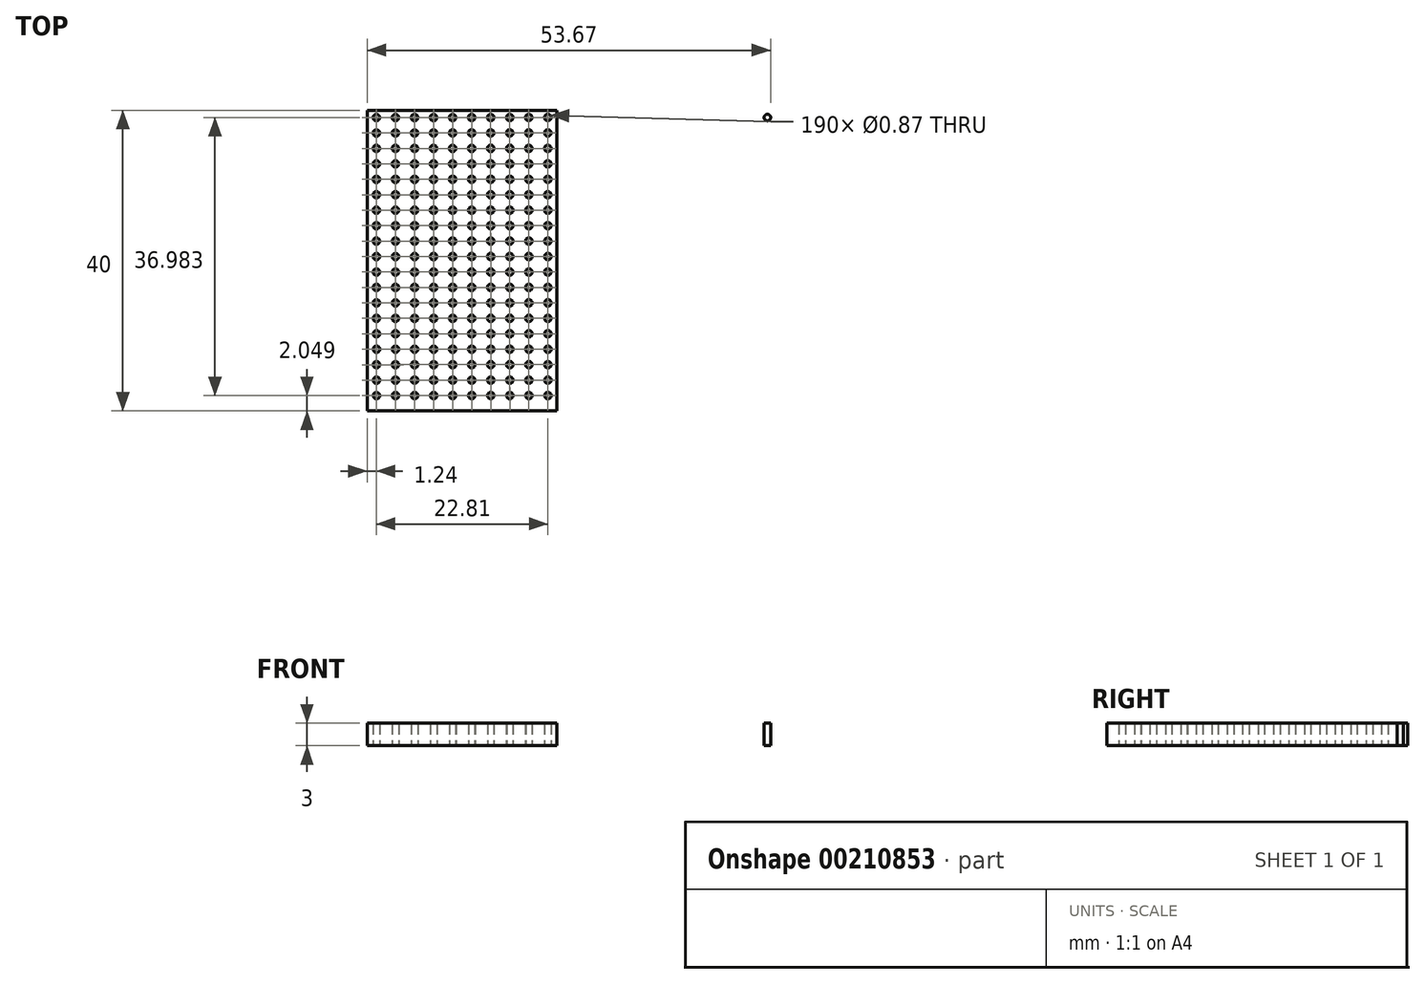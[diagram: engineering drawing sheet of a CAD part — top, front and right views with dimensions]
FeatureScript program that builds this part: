
annotation { "Feature Type Name" : "Feature", "Feature Type Description" : "" }
export const myFeature = defineFeature(function(context is Context, id is Id, definition is map)
    precondition{}
    {
        {
            var Q0;
            Q0=qCreatedBy(makeId("Top.planeOp"),FACE);
            var sketch = newSketch(context, id + "F0", { "sketchPlane" : qUnion([Q0])});
            skCircle(sketch, "E0", {"center": v(0, 0) * mm, "radius": 35 * mm, "construction": true});
            skLineSegment(sketch, "E1.bottom", {"start": v(-2, -20) * mm, "end": v(-27.24, -20) * mm});
            skLineSegment(sketch, "E1.top", {"start": v(-2, 20) * mm, "end": v(-27.24, 20) * mm});
            skLineSegment(sketch, "E1.left", {"start": v(-2, -20) * mm, "end": v(-2, 20) * mm});
            skLineSegment(sketch, "E1.right", {"start": v(-27.24, -20) * mm, "end": v(-27.24, 20) * mm});
            skPoint(sketch, "E1.middle", {"position": v(-14.62, 0) * mm});
            skPoint(sketch, "E2.middle", {"position": v(14.62, 0) * mm});
            skCircle(sketch, "E3", {"center": v(-26, 19.03) * mm, "radius": 0.43 * mm});
            skCircle(sketch, "E4.1.0.0", {"center": v(-23.47, 19.03) * mm, "radius": 0.43 * mm});
            skCircle(sketch, "E4.2.0.0", {"center": v(-20.93, 19.03) * mm, "radius": 0.43 * mm});
            skCircle(sketch, "E4.3.0.0", {"center": v(-18.4, 19.03) * mm, "radius": 0.43 * mm});
            skCircle(sketch, "E4.4.0.0", {"center": v(-15.87, 19.03) * mm, "radius": 0.43 * mm});
            skCircle(sketch, "E4.5.0.0", {"center": v(-13.33, 19.03) * mm, "radius": 0.43 * mm});
            skCircle(sketch, "E4.6.0.0", {"center": v(-10.8, 19.03) * mm, "radius": 0.43 * mm});
            skCircle(sketch, "E4.7.0.0", {"center": v(-8.27, 19.03) * mm, "radius": 0.43 * mm});
            skCircle(sketch, "E4.8.0.0", {"center": v(-5.74, 19.03) * mm, "radius": 0.43 * mm});
            skCircle(sketch, "E4.9.0.0", {"center": v(-3.2, 19.03) * mm, "radius": 0.43 * mm});
            skLineSegment(sketch, "E4.direction1", {"start": v(-26, 19.03) * mm, "end": v(-23.47, 19.03) * mm, "construction": true});
            skLineSegment(sketch, "E5.1.0.0", {"start": v(-26, 16.97) * mm, "end": v(-23.47, 16.97) * mm, "construction": true});
            skCircle(sketch, "E5.1.0.1", {"center": v(-8.27, 16.98) * mm, "radius": 0.43 * mm});
            skCircle(sketch, "E5.1.0.2", {"center": v(-3.2, 16.98) * mm, "radius": 0.43 * mm});
            skCircle(sketch, "E5.1.0.3", {"center": v(-18.4, 16.97) * mm, "radius": 0.43 * mm});
            skCircle(sketch, "E5.1.0.4", {"center": v(-20.93, 16.97) * mm, "radius": 0.43 * mm});
            skCircle(sketch, "E5.1.0.5", {"center": v(-5.73, 16.98) * mm, "radius": 0.43 * mm});
            skCircle(sketch, "E5.1.0.6", {"center": v(-10.8, 16.98) * mm, "radius": 0.43 * mm});
            skCircle(sketch, "E5.1.0.7", {"center": v(-13.33, 16.97) * mm, "radius": 0.43 * mm});
            skCircle(sketch, "E5.1.0.8", {"center": v(-15.87, 16.97) * mm, "radius": 0.43 * mm});
            skCircle(sketch, "E5.1.0.9", {"center": v(-23.47, 16.97) * mm, "radius": 0.43 * mm});
            skCircle(sketch, "E5.1.0.10", {"center": v(-26, 16.97) * mm, "radius": 0.43 * mm});
            skLineSegment(sketch, "E5.2.0.0", {"start": v(-26, 14.92) * mm, "end": v(-23.47, 14.92) * mm, "construction": true});
            skCircle(sketch, "E5.2.0.1", {"center": v(-8.27, 14.92) * mm, "radius": 0.43 * mm});
            skCircle(sketch, "E5.2.0.2", {"center": v(-3.2, 14.92) * mm, "radius": 0.43 * mm});
            skCircle(sketch, "E5.2.0.3", {"center": v(-18.4, 14.92) * mm, "radius": 0.43 * mm});
            skCircle(sketch, "E5.2.0.4", {"center": v(-20.93, 14.92) * mm, "radius": 0.43 * mm});
            skCircle(sketch, "E5.2.0.5", {"center": v(-5.73, 14.92) * mm, "radius": 0.43 * mm});
            skCircle(sketch, "E5.2.0.6", {"center": v(-10.8, 14.92) * mm, "radius": 0.43 * mm});
            skCircle(sketch, "E5.2.0.7", {"center": v(-13.33, 14.92) * mm, "radius": 0.43 * mm});
            skCircle(sketch, "E5.2.0.8", {"center": v(-15.87, 14.92) * mm, "radius": 0.43 * mm});
            skCircle(sketch, "E5.2.0.9", {"center": v(-23.47, 14.92) * mm, "radius": 0.43 * mm});
            skCircle(sketch, "E5.2.0.10", {"center": v(-26, 14.92) * mm, "radius": 0.43 * mm});
            skLineSegment(sketch, "E5.3.0.0", {"start": v(-26, 12.86) * mm, "end": v(-23.47, 12.86) * mm, "construction": true});
            skCircle(sketch, "E5.3.0.1", {"center": v(-8.27, 12.87) * mm, "radius": 0.43 * mm});
            skCircle(sketch, "E5.3.0.2", {"center": v(-3.2, 12.87) * mm, "radius": 0.43 * mm});
            skCircle(sketch, "E5.3.0.3", {"center": v(-18.4, 12.87) * mm, "radius": 0.43 * mm});
            skCircle(sketch, "E5.3.0.4", {"center": v(-20.93, 12.86) * mm, "radius": 0.43 * mm});
            skCircle(sketch, "E5.3.0.5", {"center": v(-5.73, 12.87) * mm, "radius": 0.43 * mm});
            skCircle(sketch, "E5.3.0.6", {"center": v(-10.8, 12.87) * mm, "radius": 0.43 * mm});
            skCircle(sketch, "E5.3.0.7", {"center": v(-13.33, 12.87) * mm, "radius": 0.43 * mm});
            skCircle(sketch, "E5.3.0.8", {"center": v(-15.87, 12.87) * mm, "radius": 0.43 * mm});
            skCircle(sketch, "E5.3.0.9", {"center": v(-23.47, 12.86) * mm, "radius": 0.43 * mm});
            skCircle(sketch, "E5.3.0.10", {"center": v(-26, 12.86) * mm, "radius": 0.43 * mm});
            skLineSegment(sketch, "E5.4.0.0", {"start": v(-26, 10.8) * mm, "end": v(-23.46, 10.8) * mm, "construction": true});
            skCircle(sketch, "E5.4.0.1", {"center": v(-8.27, 10.81) * mm, "radius": 0.43 * mm});
            skCircle(sketch, "E5.4.0.2", {"center": v(-3.2, 10.81) * mm, "radius": 0.43 * mm});
            skCircle(sketch, "E5.4.0.3", {"center": v(-18.4, 10.81) * mm, "radius": 0.43 * mm});
            skCircle(sketch, "E5.4.0.4", {"center": v(-20.93, 10.81) * mm, "radius": 0.43 * mm});
            skCircle(sketch, "E5.4.0.5", {"center": v(-5.73, 10.81) * mm, "radius": 0.43 * mm});
            skCircle(sketch, "E5.4.0.6", {"center": v(-10.8, 10.81) * mm, "radius": 0.43 * mm});
            skCircle(sketch, "E5.4.0.7", {"center": v(-13.33, 10.81) * mm, "radius": 0.43 * mm});
            skCircle(sketch, "E5.4.0.8", {"center": v(-15.87, 10.81) * mm, "radius": 0.43 * mm});
            skCircle(sketch, "E5.4.0.9", {"center": v(-23.46, 10.8) * mm, "radius": 0.43 * mm});
            skCircle(sketch, "E5.4.0.10", {"center": v(-26, 10.8) * mm, "radius": 0.43 * mm});
            skLineSegment(sketch, "E5.5.0.0", {"start": v(-26, 8.76) * mm, "end": v(-23.46, 8.76) * mm, "construction": true});
            skCircle(sketch, "E5.5.0.1", {"center": v(-8.27, 8.76) * mm, "radius": 0.43 * mm});
            skCircle(sketch, "E5.5.0.2", {"center": v(-3.2, 8.76) * mm, "radius": 0.43 * mm});
            skCircle(sketch, "E5.5.0.3", {"center": v(-18.4, 8.76) * mm, "radius": 0.43 * mm});
            skCircle(sketch, "E5.5.0.4", {"center": v(-20.93, 8.76) * mm, "radius": 0.43 * mm});
            skCircle(sketch, "E5.5.0.5", {"center": v(-5.73, 8.76) * mm, "radius": 0.43 * mm});
            skCircle(sketch, "E5.5.0.6", {"center": v(-10.8, 8.76) * mm, "radius": 0.43 * mm});
            skCircle(sketch, "E5.5.0.7", {"center": v(-13.33, 8.76) * mm, "radius": 0.43 * mm});
            skCircle(sketch, "E5.5.0.8", {"center": v(-15.86, 8.76) * mm, "radius": 0.43 * mm});
            skCircle(sketch, "E5.5.0.9", {"center": v(-23.46, 8.76) * mm, "radius": 0.43 * mm});
            skCircle(sketch, "E5.5.0.10", {"center": v(-26, 8.76) * mm, "radius": 0.43 * mm});
            skLineSegment(sketch, "E5.6.0.0", {"start": v(-26, 6.7) * mm, "end": v(-23.46, 6.7) * mm, "construction": true});
            skCircle(sketch, "E5.6.0.1", {"center": v(-8.26, 6.7) * mm, "radius": 0.43 * mm});
            skCircle(sketch, "E5.6.0.2", {"center": v(-3.2, 6.7) * mm, "radius": 0.43 * mm});
            skCircle(sketch, "E5.6.0.3", {"center": v(-18.4, 6.7) * mm, "radius": 0.43 * mm});
            skCircle(sketch, "E5.6.0.4", {"center": v(-20.93, 6.7) * mm, "radius": 0.43 * mm});
            skCircle(sketch, "E5.6.0.5", {"center": v(-5.73, 6.7) * mm, "radius": 0.43 * mm});
            skCircle(sketch, "E5.6.0.6", {"center": v(-10.8, 6.7) * mm, "radius": 0.43 * mm});
            skCircle(sketch, "E5.6.0.7", {"center": v(-13.33, 6.7) * mm, "radius": 0.43 * mm});
            skCircle(sketch, "E5.6.0.8", {"center": v(-15.86, 6.7) * mm, "radius": 0.43 * mm});
            skCircle(sketch, "E5.6.0.9", {"center": v(-23.46, 6.7) * mm, "radius": 0.43 * mm});
            skCircle(sketch, "E5.6.0.10", {"center": v(-26, 6.7) * mm, "radius": 0.43 * mm});
            skLineSegment(sketch, "E5.7.0.0", {"start": v(-26, 4.65) * mm, "end": v(-23.46, 4.65) * mm, "construction": true});
            skCircle(sketch, "E5.7.0.1", {"center": v(-8.26, 4.65) * mm, "radius": 0.43 * mm});
            skCircle(sketch, "E5.7.0.2", {"center": v(-3.2, 4.65) * mm, "radius": 0.43 * mm});
            skCircle(sketch, "E5.7.0.3", {"center": v(-18.4, 4.65) * mm, "radius": 0.43 * mm});
            skCircle(sketch, "E5.7.0.4", {"center": v(-20.93, 4.65) * mm, "radius": 0.43 * mm});
            skCircle(sketch, "E5.7.0.5", {"center": v(-5.73, 4.65) * mm, "radius": 0.43 * mm});
            skCircle(sketch, "E5.7.0.6", {"center": v(-10.8, 4.65) * mm, "radius": 0.43 * mm});
            skCircle(sketch, "E5.7.0.7", {"center": v(-13.33, 4.65) * mm, "radius": 0.43 * mm});
            skCircle(sketch, "E5.7.0.8", {"center": v(-15.86, 4.65) * mm, "radius": 0.43 * mm});
            skCircle(sketch, "E5.7.0.9", {"center": v(-23.46, 4.65) * mm, "radius": 0.43 * mm});
            skCircle(sketch, "E5.7.0.10", {"center": v(-26, 4.65) * mm, "radius": 0.43 * mm});
            skLineSegment(sketch, "E5.8.0.0", {"start": v(-26, 2.6) * mm, "end": v(-23.46, 2.6) * mm, "construction": true});
            skCircle(sketch, "E5.8.0.1", {"center": v(-8.26, 2.6) * mm, "radius": 0.43 * mm});
            skCircle(sketch, "E5.8.0.2", {"center": v(-3.2, 2.6) * mm, "radius": 0.43 * mm});
            skCircle(sketch, "E5.8.0.3", {"center": v(-18.4, 2.6) * mm, "radius": 0.43 * mm});
            skCircle(sketch, "E5.8.0.4", {"center": v(-20.93, 2.6) * mm, "radius": 0.43 * mm});
            skCircle(sketch, "E5.8.0.5", {"center": v(-5.73, 2.6) * mm, "radius": 0.43 * mm});
            skCircle(sketch, "E5.8.0.6", {"center": v(-10.8, 2.6) * mm, "radius": 0.43 * mm});
            skCircle(sketch, "E5.8.0.7", {"center": v(-13.33, 2.6) * mm, "radius": 0.43 * mm});
            skCircle(sketch, "E5.8.0.8", {"center": v(-15.86, 2.6) * mm, "radius": 0.43 * mm});
            skCircle(sketch, "E5.8.0.9", {"center": v(-23.46, 2.6) * mm, "radius": 0.43 * mm});
            skCircle(sketch, "E5.8.0.10", {"center": v(-26, 2.6) * mm, "radius": 0.43 * mm});
            skLineSegment(sketch, "E5.9.0.0", {"start": v(-26, 0.54) * mm, "end": v(-23.46, 0.54) * mm, "construction": true});
            skCircle(sketch, "E5.9.0.1", {"center": v(-8.26, 0.54) * mm, "radius": 0.43 * mm});
            skCircle(sketch, "E5.9.0.2", {"center": v(-3.2, 0.54) * mm, "radius": 0.43 * mm});
            skCircle(sketch, "E5.9.0.3", {"center": v(-18.4, 0.54) * mm, "radius": 0.43 * mm});
            skCircle(sketch, "E5.9.0.4", {"center": v(-20.93, 0.54) * mm, "radius": 0.43 * mm});
            skCircle(sketch, "E5.9.0.5", {"center": v(-5.73, 0.54) * mm, "radius": 0.43 * mm});
            skCircle(sketch, "E5.9.0.6", {"center": v(-10.8, 0.54) * mm, "radius": 0.43 * mm});
            skCircle(sketch, "E5.9.0.7", {"center": v(-13.33, 0.54) * mm, "radius": 0.43 * mm});
            skCircle(sketch, "E5.9.0.8", {"center": v(-15.86, 0.54) * mm, "radius": 0.43 * mm});
            skCircle(sketch, "E5.9.0.9", {"center": v(-23.46, 0.54) * mm, "radius": 0.43 * mm});
            skCircle(sketch, "E5.9.0.10", {"center": v(-26, 0.54) * mm, "radius": 0.43 * mm});
            skLineSegment(sketch, "E5.10.0.0", {"start": v(-26, -1.52) * mm, "end": v(-23.46, -1.52) * mm, "construction": true});
            skCircle(sketch, "E5.10.0.1", {"center": v(-8.26, -1.51) * mm, "radius": 0.43 * mm});
            skCircle(sketch, "E5.10.0.2", {"center": v(-3.2, -1.51) * mm, "radius": 0.43 * mm});
            skCircle(sketch, "E5.10.0.3", {"center": v(-18.4, -1.51) * mm, "radius": 0.43 * mm});
            skCircle(sketch, "E5.10.0.4", {"center": v(-20.93, -1.52) * mm, "radius": 0.43 * mm});
            skCircle(sketch, "E5.10.0.5", {"center": v(-5.73, -1.51) * mm, "radius": 0.43 * mm});
            skCircle(sketch, "E5.10.0.6", {"center": v(-10.8, -1.51) * mm, "radius": 0.43 * mm});
            skCircle(sketch, "E5.10.0.7", {"center": v(-13.33, -1.51) * mm, "radius": 0.43 * mm});
            skCircle(sketch, "E5.10.0.8", {"center": v(-15.86, -1.51) * mm, "radius": 0.43 * mm});
            skCircle(sketch, "E5.10.0.9", {"center": v(-23.46, -1.52) * mm, "radius": 0.43 * mm});
            skCircle(sketch, "E5.10.0.10", {"center": v(-26, -1.52) * mm, "radius": 0.43 * mm});
            skLineSegment(sketch, "E5.11.0.0", {"start": v(-26, -3.57) * mm, "end": v(-23.46, -3.57) * mm, "construction": true});
            skCircle(sketch, "E5.11.0.1", {"center": v(-8.26, -3.57) * mm, "radius": 0.43 * mm});
            skCircle(sketch, "E5.11.0.2", {"center": v(-3.2, -3.57) * mm, "radius": 0.43 * mm});
            skCircle(sketch, "E5.11.0.3", {"center": v(-18.4, -3.57) * mm, "radius": 0.43 * mm});
            skCircle(sketch, "E5.11.0.4", {"center": v(-20.93, -3.57) * mm, "radius": 0.43 * mm});
            skCircle(sketch, "E5.11.0.5", {"center": v(-5.73, -3.57) * mm, "radius": 0.43 * mm});
            skCircle(sketch, "E5.11.0.6", {"center": v(-10.8, -3.57) * mm, "radius": 0.43 * mm});
            skCircle(sketch, "E5.11.0.7", {"center": v(-13.33, -3.57) * mm, "radius": 0.43 * mm});
            skCircle(sketch, "E5.11.0.8", {"center": v(-15.86, -3.57) * mm, "radius": 0.43 * mm});
            skCircle(sketch, "E5.11.0.9", {"center": v(-23.46, -3.57) * mm, "radius": 0.43 * mm});
            skCircle(sketch, "E5.11.0.10", {"center": v(-26, -3.57) * mm, "radius": 0.43 * mm});
            skLineSegment(sketch, "E5.12.0.0", {"start": v(-26, -5.63) * mm, "end": v(-23.46, -5.62) * mm, "construction": true});
            skCircle(sketch, "E5.12.0.1", {"center": v(-8.26, -5.62) * mm, "radius": 0.43 * mm});
            skCircle(sketch, "E5.12.0.2", {"center": v(-3.2, -5.62) * mm, "radius": 0.43 * mm});
            skCircle(sketch, "E5.12.0.3", {"center": v(-18.4, -5.62) * mm, "radius": 0.43 * mm});
            skCircle(sketch, "E5.12.0.4", {"center": v(-20.93, -5.62) * mm, "radius": 0.43 * mm});
            skCircle(sketch, "E5.12.0.5", {"center": v(-5.73, -5.62) * mm, "radius": 0.43 * mm});
            skCircle(sketch, "E5.12.0.6", {"center": v(-10.8, -5.62) * mm, "radius": 0.43 * mm});
            skCircle(sketch, "E5.12.0.7", {"center": v(-13.33, -5.62) * mm, "radius": 0.43 * mm});
            skCircle(sketch, "E5.12.0.8", {"center": v(-15.86, -5.62) * mm, "radius": 0.43 * mm});
            skCircle(sketch, "E5.12.0.9", {"center": v(-23.46, -5.62) * mm, "radius": 0.43 * mm});
            skCircle(sketch, "E5.12.0.10", {"center": v(-26, -5.63) * mm, "radius": 0.43 * mm});
            skLineSegment(sketch, "E5.13.0.0", {"start": v(-26, -7.68) * mm, "end": v(-23.46, -7.68) * mm, "construction": true});
            skCircle(sketch, "E5.13.0.1", {"center": v(-8.26, -7.68) * mm, "radius": 0.43 * mm});
            skCircle(sketch, "E5.13.0.2", {"center": v(-3.2, -7.67) * mm, "radius": 0.43 * mm});
            skCircle(sketch, "E5.13.0.3", {"center": v(-18.4, -7.68) * mm, "radius": 0.43 * mm});
            skCircle(sketch, "E5.13.0.4", {"center": v(-20.93, -7.68) * mm, "radius": 0.43 * mm});
            skCircle(sketch, "E5.13.0.5", {"center": v(-5.73, -7.68) * mm, "radius": 0.43 * mm});
            skCircle(sketch, "E5.13.0.6", {"center": v(-10.8, -7.68) * mm, "radius": 0.43 * mm});
            skCircle(sketch, "E5.13.0.7", {"center": v(-13.33, -7.68) * mm, "radius": 0.43 * mm});
            skCircle(sketch, "E5.13.0.8", {"center": v(-15.86, -7.68) * mm, "radius": 0.43 * mm});
            skCircle(sketch, "E5.13.0.9", {"center": v(-23.46, -7.68) * mm, "radius": 0.43 * mm});
            skCircle(sketch, "E5.13.0.10", {"center": v(-26, -7.68) * mm, "radius": 0.43 * mm});
            skLineSegment(sketch, "E5.14.0.0", {"start": v(-26, -9.73) * mm, "end": v(-23.46, -9.73) * mm, "construction": true});
            skCircle(sketch, "E5.14.0.1", {"center": v(-8.26, -9.73) * mm, "radius": 0.43 * mm});
            skCircle(sketch, "E5.14.0.2", {"center": v(-3.2, -9.73) * mm, "radius": 0.43 * mm});
            skCircle(sketch, "E5.14.0.3", {"center": v(-18.4, -9.73) * mm, "radius": 0.43 * mm});
            skCircle(sketch, "E5.14.0.4", {"center": v(-20.92, -9.73) * mm, "radius": 0.43 * mm});
            skCircle(sketch, "E5.14.0.5", {"center": v(-5.73, -9.73) * mm, "radius": 0.43 * mm});
            skCircle(sketch, "E5.14.0.6", {"center": v(-10.8, -9.73) * mm, "radius": 0.43 * mm});
            skCircle(sketch, "E5.14.0.7", {"center": v(-13.33, -9.73) * mm, "radius": 0.43 * mm});
            skCircle(sketch, "E5.14.0.8", {"center": v(-15.86, -9.73) * mm, "radius": 0.43 * mm});
            skCircle(sketch, "E5.14.0.9", {"center": v(-23.46, -9.73) * mm, "radius": 0.43 * mm});
            skCircle(sketch, "E5.14.0.10", {"center": v(-26, -9.73) * mm, "radius": 0.43 * mm});
            skLineSegment(sketch, "E5.15.0.0", {"start": v(-25.99, -11.79) * mm, "end": v(-23.46, -11.79) * mm, "construction": true});
            skCircle(sketch, "E5.15.0.1", {"center": v(-8.26, -11.78) * mm, "radius": 0.43 * mm});
            skCircle(sketch, "E5.15.0.2", {"center": v(-3.2, -11.78) * mm, "radius": 0.43 * mm});
            skCircle(sketch, "E5.15.0.3", {"center": v(-18.4, -11.79) * mm, "radius": 0.43 * mm});
            skCircle(sketch, "E5.15.0.4", {"center": v(-20.92, -11.79) * mm, "radius": 0.43 * mm});
            skCircle(sketch, "E5.15.0.5", {"center": v(-5.73, -11.78) * mm, "radius": 0.43 * mm});
            skCircle(sketch, "E5.15.0.6", {"center": v(-10.8, -11.78) * mm, "radius": 0.43 * mm});
            skCircle(sketch, "E5.15.0.7", {"center": v(-13.32, -11.79) * mm, "radius": 0.43 * mm});
            skCircle(sketch, "E5.15.0.8", {"center": v(-15.86, -11.79) * mm, "radius": 0.43 * mm});
            skCircle(sketch, "E5.15.0.9", {"center": v(-23.46, -11.79) * mm, "radius": 0.43 * mm});
            skCircle(sketch, "E5.15.0.10", {"center": v(-25.99, -11.79) * mm, "radius": 0.43 * mm});
            skLineSegment(sketch, "E5.16.0.0", {"start": v(-25.99, -13.84) * mm, "end": v(-23.46, -13.84) * mm, "construction": true});
            skCircle(sketch, "E5.16.0.1", {"center": v(-8.26, -13.84) * mm, "radius": 0.43 * mm});
            skCircle(sketch, "E5.16.0.2", {"center": v(-3.2, -13.84) * mm, "radius": 0.43 * mm});
            skCircle(sketch, "E5.16.0.3", {"center": v(-18.39, -13.84) * mm, "radius": 0.43 * mm});
            skCircle(sketch, "E5.16.0.4", {"center": v(-20.92, -13.84) * mm, "radius": 0.43 * mm});
            skCircle(sketch, "E5.16.0.5", {"center": v(-5.72, -13.84) * mm, "radius": 0.43 * mm});
            skCircle(sketch, "E5.16.0.6", {"center": v(-10.8, -13.84) * mm, "radius": 0.43 * mm});
            skCircle(sketch, "E5.16.0.7", {"center": v(-13.32, -13.84) * mm, "radius": 0.43 * mm});
            skCircle(sketch, "E5.16.0.8", {"center": v(-15.86, -13.84) * mm, "radius": 0.43 * mm});
            skCircle(sketch, "E5.16.0.9", {"center": v(-23.46, -13.84) * mm, "radius": 0.43 * mm});
            skCircle(sketch, "E5.16.0.10", {"center": v(-25.99, -13.84) * mm, "radius": 0.43 * mm});
            skLineSegment(sketch, "E5.17.0.0", {"start": v(-25.99, -15.9) * mm, "end": v(-23.46, -15.9) * mm, "construction": true});
            skCircle(sketch, "E5.17.0.1", {"center": v(-8.26, -15.9) * mm, "radius": 0.43 * mm});
            skCircle(sketch, "E5.17.0.2", {"center": v(-3.2, -15.9) * mm, "radius": 0.43 * mm});
            skCircle(sketch, "E5.17.0.3", {"center": v(-18.39, -15.9) * mm, "radius": 0.43 * mm});
            skCircle(sketch, "E5.17.0.4", {"center": v(-20.92, -15.9) * mm, "radius": 0.43 * mm});
            skCircle(sketch, "E5.17.0.5", {"center": v(-5.72, -15.9) * mm, "radius": 0.43 * mm});
            skCircle(sketch, "E5.17.0.6", {"center": v(-10.8, -15.9) * mm, "radius": 0.43 * mm});
            skCircle(sketch, "E5.17.0.7", {"center": v(-13.32, -15.9) * mm, "radius": 0.43 * mm});
            skCircle(sketch, "E5.17.0.8", {"center": v(-15.86, -15.9) * mm, "radius": 0.43 * mm});
            skCircle(sketch, "E5.17.0.9", {"center": v(-23.46, -15.9) * mm, "radius": 0.43 * mm});
            skCircle(sketch, "E5.17.0.10", {"center": v(-25.99, -15.9) * mm, "radius": 0.43 * mm});
            skLineSegment(sketch, "E5.18.0.0", {"start": v(-25.99, -17.95) * mm, "end": v(-23.45, -17.95) * mm, "construction": true});
            skCircle(sketch, "E5.18.0.1", {"center": v(-8.26, -17.95) * mm, "radius": 0.43 * mm});
            skCircle(sketch, "E5.18.0.2", {"center": v(-3.2, -17.95) * mm, "radius": 0.43 * mm});
            skCircle(sketch, "E5.18.0.3", {"center": v(-18.39, -17.95) * mm, "radius": 0.43 * mm});
            skCircle(sketch, "E5.18.0.4", {"center": v(-20.92, -17.95) * mm, "radius": 0.43 * mm});
            skCircle(sketch, "E5.18.0.5", {"center": v(-5.72, -17.95) * mm, "radius": 0.43 * mm});
            skCircle(sketch, "E5.18.0.6", {"center": v(-10.79, -17.95) * mm, "radius": 0.43 * mm});
            skCircle(sketch, "E5.18.0.7", {"center": v(-13.32, -17.95) * mm, "radius": 0.43 * mm});
            skCircle(sketch, "E5.18.0.8", {"center": v(-15.86, -17.95) * mm, "radius": 0.43 * mm});
            skCircle(sketch, "E5.18.0.9", {"center": v(-23.45, -17.95) * mm, "radius": 0.43 * mm});
            skCircle(sketch, "E5.18.0.10", {"center": v(-25.99, -17.95) * mm, "radius": 0.43 * mm});
            skLineSegment(sketch, "E5.direction1", {"start": v(-26, 19.03) * mm, "end": v(-26, 16.97) * mm, "construction": true});
            skPoint(sketch, "E2.left.end.orphan", {"position": v(27.24, 20) * mm});
            skPoint(sketch, "E2.bottom.start.orphan", {"position": v(27.24, -20) * mm});
            skPoint(sketch, "E2.right.end.orphan", {"position": v(2, 20) * mm});
            skPoint(sketch, "E2.right.start.orphan", {"position": v(2, -20) * mm});
            skCircle(sketch, "E6.MirrorC", {"center": v(26, 19.03) * mm, "radius": 0.43 * mm});
            skCircle(sketch, "E7.MirrorC", {"center": v(26, 16.97) * mm, "radius": 0.43 * mm});
            skLineSegment(sketch, "E8.MirrorCS", {"start": v(26, 19.03) * mm, "end": v(26, 16.97) * mm, "construction": true});
            skCircle(sketch, "E9.MirrorC", {"center": v(26, 0.54) * mm, "radius": 0.43 * mm});
            skCircle(sketch, "E10.MirrorC", {"center": v(23.46, -5.62) * mm, "radius": 0.43 * mm});
            skLineSegment(sketch, "E11.MirrorCS", {"start": v(26, 4.65) * mm, "end": v(23.46, 4.65) * mm, "construction": true});
            skCircle(sketch, "E12.MirrorC", {"center": v(23.46, 0.54) * mm, "radius": 0.43 * mm});
            skLineSegment(sketch, "E13.MirrorCS", {"start": v(26, 10.8) * mm, "end": v(23.46, 10.8) * mm, "construction": true});
            skCircle(sketch, "E14.MirrorC", {"center": v(26, 6.7) * mm, "radius": 0.43 * mm});
            skCircle(sketch, "E15.MirrorC", {"center": v(26, 12.86) * mm, "radius": 0.43 * mm});
            skCircle(sketch, "E16.MirrorC", {"center": v(23.46, 6.7) * mm, "radius": 0.43 * mm});
            skLineSegment(sketch, "E17.MirrorCS", {"start": v(26, 16.97) * mm, "end": v(23.47, 16.97) * mm, "construction": true});
            skLineSegment(sketch, "E18.MirrorCS", {"start": v(25.99, -15.9) * mm, "end": v(23.46, -15.9) * mm, "construction": true});
            skCircle(sketch, "E19.MirrorC", {"center": v(23.47, 19.03) * mm, "radius": 0.43 * mm});
            skLineSegment(sketch, "E20.MirrorCS", {"start": v(26, 19.03) * mm, "end": v(23.47, 19.03) * mm, "construction": true});
            skLineSegment(sketch, "E21.MirrorCS", {"start": v(26, -9.73) * mm, "end": v(23.46, -9.73) * mm, "construction": true});
            skCircle(sketch, "E22.MirrorC", {"center": v(25.99, -13.84) * mm, "radius": 0.43 * mm});
            skCircle(sketch, "E23.MirrorC", {"center": v(23.47, 12.86) * mm, "radius": 0.43 * mm});
            skCircle(sketch, "E24.MirrorC", {"center": v(26, -7.68) * mm, "radius": 0.43 * mm});
            skCircle(sketch, "E25.MirrorC", {"center": v(23.46, -13.84) * mm, "radius": 0.43 * mm});
            skLineSegment(sketch, "E26.MirrorCS", {"start": v(26, -3.57) * mm, "end": v(23.46, -3.57) * mm, "construction": true});
            skCircle(sketch, "E27.MirrorC", {"center": v(26, 4.65) * mm, "radius": 0.43 * mm});
            skCircle(sketch, "E28.MirrorC", {"center": v(23.46, -1.52) * mm, "radius": 0.43 * mm});
            skLineSegment(sketch, "E29.MirrorCS", {"start": v(26, 8.76) * mm, "end": v(23.46, 8.76) * mm, "construction": true});
            skCircle(sketch, "E30.MirrorC", {"center": v(23.46, -7.68) * mm, "radius": 0.43 * mm});
            skLineSegment(sketch, "E31.MirrorCS", {"start": v(26, 2.6) * mm, "end": v(23.46, 2.6) * mm, "construction": true});
            skCircle(sketch, "E32.MirrorC", {"center": v(26, -1.52) * mm, "radius": 0.43 * mm});
            skLineSegment(sketch, "E33.MirrorCS", {"start": v(25.99, -17.95) * mm, "end": v(23.45, -17.95) * mm, "construction": true});
            skCircle(sketch, "E34.MirrorC", {"center": v(23.46, 4.65) * mm, "radius": 0.43 * mm});
            skLineSegment(sketch, "E35.MirrorCS", {"start": v(26, 14.92) * mm, "end": v(23.47, 14.92) * mm, "construction": true});
            skCircle(sketch, "E36.MirrorC", {"center": v(26, 10.8) * mm, "radius": 0.43 * mm});
            skCircle(sketch, "E37.MirrorC", {"center": v(25.99, -15.9) * mm, "radius": 0.43 * mm});
            skLineSegment(sketch, "E38.MirrorCS", {"start": v(25.99, -11.79) * mm, "end": v(23.46, -11.79) * mm, "construction": true});
            skCircle(sketch, "E39.MirrorC", {"center": v(23.46, 10.8) * mm, "radius": 0.43 * mm});
            skCircle(sketch, "E40.MirrorC", {"center": v(23.46, -15.9) * mm, "radius": 0.43 * mm});
            skLineSegment(sketch, "E41.MirrorCS", {"start": v(26, -5.63) * mm, "end": v(23.46, -5.62) * mm, "construction": true});
            skCircle(sketch, "E42.MirrorC", {"center": v(26, -9.73) * mm, "radius": 0.43 * mm});
            skCircle(sketch, "E43.MirrorC", {"center": v(23.47, 16.97) * mm, "radius": 0.43 * mm});
            skCircle(sketch, "E44.MirrorC", {"center": v(26, -3.57) * mm, "radius": 0.43 * mm});
            skCircle(sketch, "E45.MirrorC", {"center": v(23.46, -9.73) * mm, "radius": 0.43 * mm});
            skLineSegment(sketch, "E46.MirrorCS", {"start": v(26, 0.54) * mm, "end": v(23.46, 0.54) * mm, "construction": true});
            skCircle(sketch, "E47.MirrorC", {"center": v(23.46, -3.57) * mm, "radius": 0.43 * mm});
            skLineSegment(sketch, "E48.MirrorCS", {"start": v(26, 6.7) * mm, "end": v(23.46, 6.7) * mm, "construction": true});
            skCircle(sketch, "E49.MirrorC", {"center": v(26, 2.6) * mm, "radius": 0.43 * mm});
            skLineSegment(sketch, "E50.MirrorCS", {"start": v(26, -1.52) * mm, "end": v(23.46, -1.52) * mm, "construction": true});
            skCircle(sketch, "E51.MirrorC", {"center": v(23.46, -11.79) * mm, "radius": 0.43 * mm});
            skCircle(sketch, "E52.MirrorC", {"center": v(26, -5.63) * mm, "radius": 0.43 * mm});
            skCircle(sketch, "E53.MirrorC", {"center": v(23.46, 8.76) * mm, "radius": 0.43 * mm});
            skCircle(sketch, "E54.MirrorC", {"center": v(26, 14.92) * mm, "radius": 0.43 * mm});
            skCircle(sketch, "E55.MirrorC", {"center": v(25.99, -17.95) * mm, "radius": 0.43 * mm});
            skLineSegment(sketch, "E56.MirrorCS", {"start": v(25.99, -13.84) * mm, "end": v(23.46, -13.84) * mm, "construction": true});
            skCircle(sketch, "E57.MirrorC", {"center": v(26, 8.76) * mm, "radius": 0.43 * mm});
            skLineSegment(sketch, "E58.MirrorCS", {"start": v(26, 12.86) * mm, "end": v(23.47, 12.86) * mm, "construction": true});
            skCircle(sketch, "E59.MirrorC", {"center": v(23.46, 2.6) * mm, "radius": 0.43 * mm});
            skCircle(sketch, "E60.MirrorC", {"center": v(23.45, -17.95) * mm, "radius": 0.43 * mm});
            skCircle(sketch, "E61.MirrorC", {"center": v(23.47, 14.92) * mm, "radius": 0.43 * mm});
            skCircle(sketch, "E62.MirrorC", {"center": v(25.99, -11.79) * mm, "radius": 0.43 * mm});
            skLineSegment(sketch, "E63.MirrorCS", {"start": v(26, -7.68) * mm, "end": v(23.46, -7.68) * mm, "construction": true});
            skCircle(sketch, "E64.MirrorC", {"center": v(3.2, -15.9) * mm, "radius": 0.43 * mm});
            skCircle(sketch, "E65.MirrorC", {"center": v(13.32, -17.95) * mm, "radius": 0.43 * mm});
            skCircle(sketch, "E66.MirrorC", {"center": v(5.73, 2.6) * mm, "radius": 0.43 * mm});
            skCircle(sketch, "E67.MirrorC", {"center": v(20.93, -3.57) * mm, "radius": 0.43 * mm});
            skCircle(sketch, "E68.MirrorC", {"center": v(13.33, 14.92) * mm, "radius": 0.43 * mm});
            skCircle(sketch, "E69.MirrorC", {"center": v(8.27, 10.81) * mm, "radius": 0.43 * mm});
            skCircle(sketch, "E70.MirrorC", {"center": v(10.8, 8.76) * mm, "radius": 0.43 * mm});
            skCircle(sketch, "E71.MirrorC", {"center": v(3.2, 16.98) * mm, "radius": 0.43 * mm});
            skCircle(sketch, "E72.MirrorC", {"center": v(20.93, 2.6) * mm, "radius": 0.43 * mm});
            skCircle(sketch, "E73.MirrorC", {"center": v(18.4, -3.57) * mm, "radius": 0.43 * mm});
            skCircle(sketch, "E74.MirrorC", {"center": v(15.86, -5.62) * mm, "radius": 0.43 * mm});
            skCircle(sketch, "E75.MirrorC", {"center": v(10.8, 14.92) * mm, "radius": 0.43 * mm});
            skCircle(sketch, "E76.MirrorC", {"center": v(5.73, 8.76) * mm, "radius": 0.43 * mm});
            skCircle(sketch, "E77.MirrorC", {"center": v(8.27, 16.98) * mm, "radius": 0.43 * mm});
            skCircle(sketch, "E78.MirrorC", {"center": v(3.2, -9.73) * mm, "radius": 0.43 * mm});
            skCircle(sketch, "E79.MirrorC", {"center": v(13.32, -11.79) * mm, "radius": 0.43 * mm});
            skCircle(sketch, "E80.MirrorC", {"center": v(8.26, -15.9) * mm, "radius": 0.43 * mm});
            skCircle(sketch, "E81.MirrorC", {"center": v(10.79, -17.95) * mm, "radius": 0.43 * mm});
            skCircle(sketch, "E82.MirrorC", {"center": v(5.73, 14.92) * mm, "radius": 0.43 * mm});
            skCircle(sketch, "E83.MirrorC", {"center": v(20.93, 8.76) * mm, "radius": 0.43 * mm});
            skCircle(sketch, "E84.MirrorC", {"center": v(8.26, -9.73) * mm, "radius": 0.43 * mm});
            skCircle(sketch, "E85.MirrorC", {"center": v(10.8, -11.78) * mm, "radius": 0.43 * mm});
            skCircle(sketch, "E86.MirrorC", {"center": v(5.72, -17.95) * mm, "radius": 0.43 * mm});
            skCircle(sketch, "E87.MirrorC", {"center": v(18.4, 2.6) * mm, "radius": 0.43 * mm});
            skCircle(sketch, "E88.MirrorC", {"center": v(15.86, 0.54) * mm, "radius": 0.43 * mm});
            skCircle(sketch, "E89.MirrorC", {"center": v(3.2, -3.57) * mm, "radius": 0.43 * mm});
            skCircle(sketch, "E90.MirrorC", {"center": v(13.33, -5.62) * mm, "radius": 0.43 * mm});
            skCircle(sketch, "E91.MirrorC", {"center": v(8.27, 19.03) * mm, "radius": 0.43 * mm});
            skCircle(sketch, "E92.MirrorC", {"center": v(10.8, 19.03) * mm, "radius": 0.43 * mm});
            skCircle(sketch, "E93.MirrorC", {"center": v(13.33, 19.03) * mm, "radius": 0.43 * mm});
            skCircle(sketch, "E94.MirrorC", {"center": v(15.87, 19.03) * mm, "radius": 0.43 * mm});
            skCircle(sketch, "E95.MirrorC", {"center": v(18.4, 19.03) * mm, "radius": 0.43 * mm});
            skCircle(sketch, "E96.MirrorC", {"center": v(20.93, 19.03) * mm, "radius": 0.43 * mm});
            skCircle(sketch, "E97.MirrorC", {"center": v(3.2, 19.03) * mm, "radius": 0.43 * mm});
            skCircle(sketch, "E98.MirrorC", {"center": v(5.74, 19.03) * mm, "radius": 0.43 * mm});
            skCircle(sketch, "E99.MirrorC", {"center": v(5.73, -11.78) * mm, "radius": 0.43 * mm});
            skCircle(sketch, "E100.MirrorC", {"center": v(20.92, -17.95) * mm, "radius": 0.43 * mm});
            skCircle(sketch, "E101.MirrorC", {"center": v(3.2, 2.6) * mm, "radius": 0.43 * mm});
            skCircle(sketch, "E102.MirrorC", {"center": v(13.33, 0.54) * mm, "radius": 0.43 * mm});
            skCircle(sketch, "E103.MirrorC", {"center": v(8.26, -3.57) * mm, "radius": 0.43 * mm});
            skCircle(sketch, "E104.MirrorC", {"center": v(10.8, -5.62) * mm, "radius": 0.43 * mm});
            skCircle(sketch, "E105.MirrorC", {"center": v(20.93, 14.92) * mm, "radius": 0.43 * mm});
            skCircle(sketch, "E106.MirrorC", {"center": v(18.4, 8.76) * mm, "radius": 0.43 * mm});
            skCircle(sketch, "E107.MirrorC", {"center": v(15.86, 6.7) * mm, "radius": 0.43 * mm});
            skCircle(sketch, "E108.MirrorC", {"center": v(20.92, -11.79) * mm, "radius": 0.43 * mm});
            skCircle(sketch, "E109.MirrorC", {"center": v(18.39, -17.95) * mm, "radius": 0.43 * mm});
            skCircle(sketch, "E110.MirrorC", {"center": v(8.26, 2.6) * mm, "radius": 0.43 * mm});
            skCircle(sketch, "E111.MirrorC", {"center": v(10.8, 0.54) * mm, "radius": 0.43 * mm});
            skCircle(sketch, "E112.MirrorC", {"center": v(5.73, -5.62) * mm, "radius": 0.43 * mm});
            skCircle(sketch, "E113.MirrorC", {"center": v(18.4, 14.92) * mm, "radius": 0.43 * mm});
            skCircle(sketch, "E114.MirrorC", {"center": v(15.87, 12.87) * mm, "radius": 0.43 * mm});
            skCircle(sketch, "E115.MirrorC", {"center": v(3.2, 8.76) * mm, "radius": 0.43 * mm});
            skCircle(sketch, "E116.MirrorC", {"center": v(13.33, 6.7) * mm, "radius": 0.43 * mm});
            skCircle(sketch, "E117.MirrorC", {"center": v(8.26, -17.95) * mm, "radius": 0.43 * mm});
            skCircle(sketch, "E118.MirrorC", {"center": v(18.4, -5.62) * mm, "radius": 0.43 * mm});
            skCircle(sketch, "E119.MirrorC", {"center": v(15.86, -7.68) * mm, "radius": 0.43 * mm});
            skCircle(sketch, "E120.MirrorC", {"center": v(3.2, -11.78) * mm, "radius": 0.43 * mm});
            skCircle(sketch, "E121.MirrorC", {"center": v(13.32, -13.84) * mm, "radius": 0.43 * mm});
            skCircle(sketch, "E122.MirrorC", {"center": v(5.73, 6.7) * mm, "radius": 0.43 * mm});
            skCircle(sketch, "E123.MirrorC", {"center": v(20.93, 0.54) * mm, "radius": 0.43 * mm});
            skCircle(sketch, "E124.MirrorC", {"center": v(8.27, 14.92) * mm, "radius": 0.43 * mm});
            skCircle(sketch, "E125.MirrorC", {"center": v(10.8, 12.87) * mm, "radius": 0.43 * mm});
            skCircle(sketch, "E126.MirrorC", {"center": v(18.4, -11.79) * mm, "radius": 0.43 * mm});
            skCircle(sketch, "E127.MirrorC", {"center": v(15.86, -13.84) * mm, "radius": 0.43 * mm});
            skCircle(sketch, "E128.MirrorC", {"center": v(3.2, -17.95) * mm, "radius": 0.43 * mm});
            skCircle(sketch, "E129.MirrorC", {"center": v(5.73, 0.54) * mm, "radius": 0.43 * mm});
            skCircle(sketch, "E130.MirrorC", {"center": v(20.93, -5.62) * mm, "radius": 0.43 * mm});
            skCircle(sketch, "E131.MirrorC", {"center": v(3.2, 14.92) * mm, "radius": 0.43 * mm});
            skCircle(sketch, "E132.MirrorC", {"center": v(13.33, 12.87) * mm, "radius": 0.43 * mm});
            skCircle(sketch, "E133.MirrorC", {"center": v(8.27, 8.76) * mm, "radius": 0.43 * mm});
            skCircle(sketch, "E134.MirrorC", {"center": v(10.8, 6.7) * mm, "radius": 0.43 * mm});
            skCircle(sketch, "E135.MirrorC", {"center": v(3.2, -5.62) * mm, "radius": 0.43 * mm});
            skCircle(sketch, "E136.MirrorC", {"center": v(13.33, -7.68) * mm, "radius": 0.43 * mm});
            skCircle(sketch, "E137.MirrorC", {"center": v(8.26, -11.78) * mm, "radius": 0.43 * mm});
            skCircle(sketch, "E138.MirrorC", {"center": v(10.8, -13.84) * mm, "radius": 0.43 * mm});
            skCircle(sketch, "E139.MirrorC", {"center": v(20.93, 6.7) * mm, "radius": 0.43 * mm});
            skCircle(sketch, "E140.MirrorC", {"center": v(18.4, 0.54) * mm, "radius": 0.43 * mm});
            skCircle(sketch, "E141.MirrorC", {"center": v(15.86, -1.51) * mm, "radius": 0.43 * mm});
            skCircle(sketch, "E142.MirrorC", {"center": v(5.73, 12.87) * mm, "radius": 0.43 * mm});
            skCircle(sketch, "E143.MirrorC", {"center": v(8.26, -5.62) * mm, "radius": 0.43 * mm});
            skCircle(sketch, "E144.MirrorC", {"center": v(10.8, -7.68) * mm, "radius": 0.43 * mm});
            skCircle(sketch, "E145.MirrorC", {"center": v(5.72, -13.84) * mm, "radius": 0.43 * mm});
            skCircle(sketch, "E146.MirrorC", {"center": v(18.4, 6.7) * mm, "radius": 0.43 * mm});
            skCircle(sketch, "E147.MirrorC", {"center": v(15.86, 4.65) * mm, "radius": 0.43 * mm});
            skCircle(sketch, "E148.MirrorC", {"center": v(3.2, 0.54) * mm, "radius": 0.43 * mm});
            skCircle(sketch, "E149.MirrorC", {"center": v(13.33, -1.51) * mm, "radius": 0.43 * mm});
            skCircle(sketch, "E150.MirrorC", {"center": v(20.93, 12.86) * mm, "radius": 0.43 * mm});
            skCircle(sketch, "E151.MirrorC", {"center": v(5.73, -7.68) * mm, "radius": 0.43 * mm});
            skCircle(sketch, "E152.MirrorC", {"center": v(20.92, -13.84) * mm, "radius": 0.43 * mm});
            skCircle(sketch, "E153.MirrorC", {"center": v(3.2, 6.7) * mm, "radius": 0.43 * mm});
            skCircle(sketch, "E154.MirrorC", {"center": v(13.33, 4.65) * mm, "radius": 0.43 * mm});
            skCircle(sketch, "E155.MirrorC", {"center": v(8.26, 0.54) * mm, "radius": 0.43 * mm});
            skCircle(sketch, "E156.MirrorC", {"center": v(10.8, -1.51) * mm, "radius": 0.43 * mm});
            skCircle(sketch, "E157.MirrorC", {"center": v(18.4, 12.87) * mm, "radius": 0.43 * mm});
            skCircle(sketch, "E158.MirrorC", {"center": v(15.87, 10.81) * mm, "radius": 0.43 * mm});
            skCircle(sketch, "E159.MirrorC", {"center": v(15.86, -15.9) * mm, "radius": 0.43 * mm});
            skCircle(sketch, "E160.MirrorC", {"center": v(20.93, -7.68) * mm, "radius": 0.43 * mm});
            skCircle(sketch, "E161.MirrorC", {"center": v(18.39, -13.84) * mm, "radius": 0.43 * mm});
            skCircle(sketch, "E162.MirrorC", {"center": v(8.26, 6.7) * mm, "radius": 0.43 * mm});
            skCircle(sketch, "E163.MirrorC", {"center": v(10.8, 4.65) * mm, "radius": 0.43 * mm});
            skCircle(sketch, "E164.MirrorC", {"center": v(5.73, -1.51) * mm, "radius": 0.43 * mm});
            skCircle(sketch, "E165.MirrorC", {"center": v(15.87, 16.97) * mm, "radius": 0.43 * mm});
            skCircle(sketch, "E166.MirrorC", {"center": v(3.2, 12.87) * mm, "radius": 0.43 * mm});
            skCircle(sketch, "E167.MirrorC", {"center": v(13.33, 10.81) * mm, "radius": 0.43 * mm});
            skCircle(sketch, "E168.MirrorC", {"center": v(18.4, -9.73) * mm, "radius": 0.43 * mm});
            skCircle(sketch, "E169.MirrorC", {"center": v(13.32, -15.9) * mm, "radius": 0.43 * mm});
            skCircle(sketch, "E170.MirrorC", {"center": v(18.4, -7.68) * mm, "radius": 0.43 * mm});
            skCircle(sketch, "E171.MirrorC", {"center": v(15.86, -9.73) * mm, "radius": 0.43 * mm});
            skCircle(sketch, "E172.MirrorC", {"center": v(3.2, -13.84) * mm, "radius": 0.43 * mm});
            skCircle(sketch, "E173.MirrorC", {"center": v(5.73, 4.65) * mm, "radius": 0.43 * mm});
            skCircle(sketch, "E174.MirrorC", {"center": v(20.93, -1.52) * mm, "radius": 0.43 * mm});
            skCircle(sketch, "E175.MirrorC", {"center": v(13.33, 16.97) * mm, "radius": 0.43 * mm});
            skCircle(sketch, "E176.MirrorC", {"center": v(8.27, 12.87) * mm, "radius": 0.43 * mm});
            skCircle(sketch, "E177.MirrorC", {"center": v(10.8, 10.81) * mm, "radius": 0.43 * mm});
            skCircle(sketch, "E178.MirrorC", {"center": v(15.86, -11.79) * mm, "radius": 0.43 * mm});
            skCircle(sketch, "E179.MirrorC", {"center": v(20.92, -9.73) * mm, "radius": 0.43 * mm});
            skCircle(sketch, "E180.MirrorC", {"center": v(18.39, -15.9) * mm, "radius": 0.43 * mm});
            skCircle(sketch, "E181.MirrorC", {"center": v(15.86, -17.95) * mm, "radius": 0.43 * mm});
            skCircle(sketch, "E182.MirrorC", {"center": v(10.8, 2.6) * mm, "radius": 0.43 * mm});
            skCircle(sketch, "E183.MirrorC", {"center": v(5.73, -3.57) * mm, "radius": 0.43 * mm});
            skCircle(sketch, "E184.MirrorC", {"center": v(3.2, 10.81) * mm, "radius": 0.43 * mm});
            skCircle(sketch, "E185.MirrorC", {"center": v(15.87, 14.92) * mm, "radius": 0.43 * mm});
            skCircle(sketch, "E186.MirrorC", {"center": v(8.26, 4.65) * mm, "radius": 0.43 * mm});
            skCircle(sketch, "E187.MirrorC", {"center": v(13.33, 8.76) * mm, "radius": 0.43 * mm});
            skCircle(sketch, "E188.MirrorC", {"center": v(18.4, 16.97) * mm, "radius": 0.43 * mm});
            skCircle(sketch, "E189.MirrorC", {"center": v(5.73, 16.98) * mm, "radius": 0.43 * mm});
            skCircle(sketch, "E190.MirrorC", {"center": v(18.4, 4.65) * mm, "radius": 0.43 * mm});
            skCircle(sketch, "E191.MirrorC", {"center": v(20.93, 10.81) * mm, "radius": 0.43 * mm});
            skCircle(sketch, "E192.MirrorC", {"center": v(8.26, -7.68) * mm, "radius": 0.43 * mm});
            skCircle(sketch, "E193.MirrorC", {"center": v(13.33, -3.57) * mm, "radius": 0.43 * mm});
            skCircle(sketch, "E194.MirrorC", {"center": v(3.2, -1.51) * mm, "radius": 0.43 * mm});
            skCircle(sketch, "E195.MirrorC", {"center": v(15.86, 2.6) * mm, "radius": 0.43 * mm});
            skCircle(sketch, "E196.MirrorC", {"center": v(5.72, -15.9) * mm, "radius": 0.43 * mm});
            skCircle(sketch, "E197.MirrorC", {"center": v(10.8, -9.73) * mm, "radius": 0.43 * mm});
            skCircle(sketch, "E198.MirrorC", {"center": v(10.8, 16.98) * mm, "radius": 0.43 * mm});
            skCircle(sketch, "E199.MirrorC", {"center": v(20.93, 4.65) * mm, "radius": 0.43 * mm});
            skCircle(sketch, "E200.MirrorC", {"center": v(5.73, 10.81) * mm, "radius": 0.43 * mm});
            skCircle(sketch, "E201.MirrorC", {"center": v(3.2, -7.67) * mm, "radius": 0.43 * mm});
            skCircle(sketch, "E202.MirrorC", {"center": v(15.86, -3.57) * mm, "radius": 0.43 * mm});
            skCircle(sketch, "E203.MirrorC", {"center": v(20.93, 16.97) * mm, "radius": 0.43 * mm});
            skCircle(sketch, "E204.MirrorC", {"center": v(18.4, -1.51) * mm, "radius": 0.43 * mm});
            skCircle(sketch, "E205.MirrorC", {"center": v(3.2, 4.65) * mm, "radius": 0.43 * mm});
            skCircle(sketch, "E206.MirrorC", {"center": v(15.86, 8.76) * mm, "radius": 0.43 * mm});
            skCircle(sketch, "E207.MirrorC", {"center": v(18.4, 10.81) * mm, "radius": 0.43 * mm});
            skCircle(sketch, "E208.MirrorC", {"center": v(10.8, -3.57) * mm, "radius": 0.43 * mm});
            skCircle(sketch, "E209.MirrorC", {"center": v(13.33, -9.73) * mm, "radius": 0.43 * mm});
            skCircle(sketch, "E210.MirrorC", {"center": v(8.26, -1.51) * mm, "radius": 0.43 * mm});
            skCircle(sketch, "E211.MirrorC", {"center": v(13.33, 2.6) * mm, "radius": 0.43 * mm});
            skCircle(sketch, "E212.MirrorC", {"center": v(10.8, -15.9) * mm, "radius": 0.43 * mm});
            skCircle(sketch, "E213.MirrorC", {"center": v(20.92, -15.9) * mm, "radius": 0.43 * mm});
            skCircle(sketch, "E214.MirrorC", {"center": v(8.26, -13.84) * mm, "radius": 0.43 * mm});
            skCircle(sketch, "E215.MirrorC", {"center": v(5.73, -9.73) * mm, "radius": 0.43 * mm});
            skLineSegment(sketch, "E216.MirrorCS", {"start": v(27.24, -20) * mm, "end": v(27.24, 20) * mm});
            skLineSegment(sketch, "E217.MirrorCS", {"start": v(2, -20) * mm, "end": v(2, 20) * mm});
            skLineSegment(sketch, "E218.MirrorCS", {"start": v(2, 20) * mm, "end": v(27.24, 20) * mm});
            skLineSegment(sketch, "E219.MirrorCS", {"start": v(2, -20) * mm, "end": v(27.24, -20) * mm});
            skSolve(sketch);
        }
        {
            var Q0;
            Q0=makeQuery(id+"F0.imprint","IMPRINT",FACE,{"disambiguationData":[TD([[makeQuery(id+"F0.imprint","IMPRINT",EDGE,{"derivedFrom":sQuery(id+"F0.wireOp",EDGE,"E1.bottom")}),-1.0]])]});
            var Q1;
            Q1=makeQuery(id+"F0.imprint","IMPRINT",FACE,{"disambiguationData":[TD([[makeQuery(id+"F0.imprint","IMPRINT",EDGE,{"derivedFrom":sQuery(id+"F0.wireOp",EDGE,"E6.MirrorC")}),1.0]])]});
            extrude(context, id + "F1", {"entities" : qUnion([Q0, Q1]), "depth" : 3 * mm});
        }
    });
